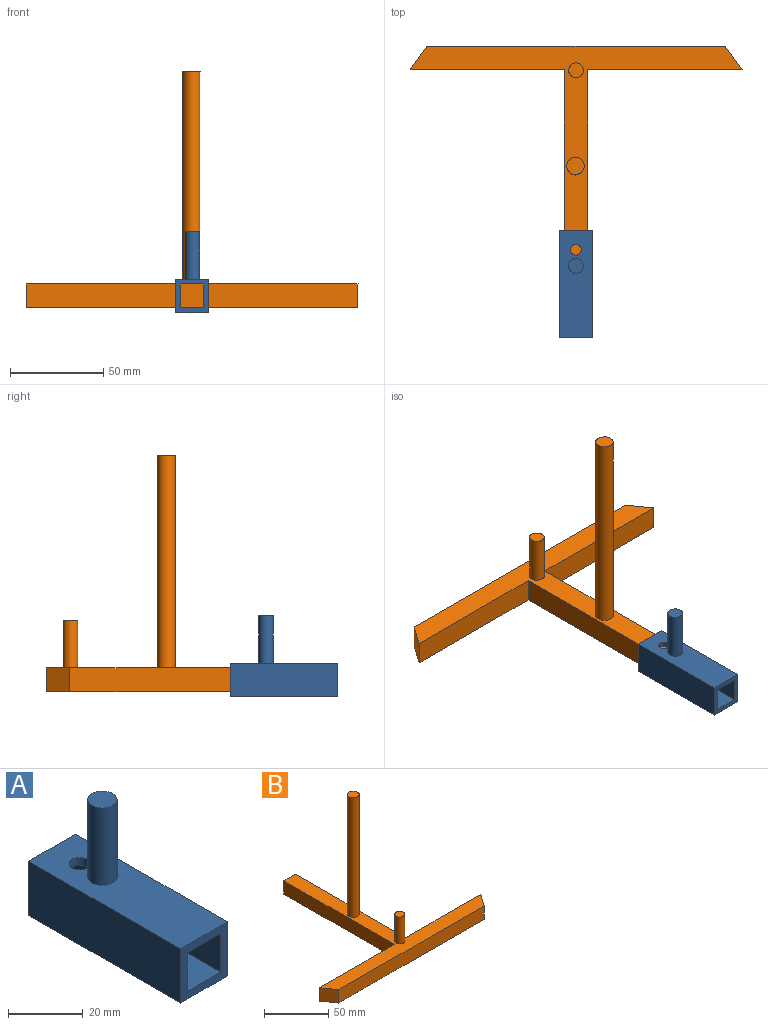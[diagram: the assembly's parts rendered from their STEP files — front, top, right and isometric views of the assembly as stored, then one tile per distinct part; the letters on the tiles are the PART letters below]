
ASSEMBLY  parts=2 mates=1
PART A: 13 faces, bbox 17.8x57.7x43.2 mm
  f0: plane 57.66x12.7mm, normal (0,0,-1), area 706.4mm2, adj f1,f7,f8,f9,f12
  f1: plane 57.66x12.7mm, normal (-1,0,0), area 732.3mm2, adj f0,f2,f8,f9
  f2: plane 57.66x12.7mm, normal (0,0,1), area 732.3mm2, adj f1,f7,f8,f9
  f3: plane 57.66x17.78mm, normal (0,0,1), area 950mm2, adj f4,f6,f8,f9,f10,f12
  f4: plane 57.66x17.78mm, normal (-1,0,0), area 1025.2mm2, adj f3,f5,f8,f9
  f5: plane 57.66x17.78mm, normal (0,0,-1), area 1025.2mm2, adj f4,f6,f8,f9
  f6: plane 57.66x17.78mm, normal (1,0,0), area 1025.2mm2, adj f3,f5,f8,f9
  f7: plane 57.66x12.7mm, normal (1,0,0), area 732.3mm2, adj f0,f2,f8,f9
  f8: plane 17.78x17.78mm, normal (0,-1,0), area 154.8mm2, adj f0,f1,f2,f3,f4,f5,f6,f7
  f9: plane 17.78x17.78mm, normal (0,1,0), area 154.8mm2, adj f0,f1,f2,f3,f4,f5,f6,f7
  f10: cylinder r=3.96mm len=25.4mm, axis (0,0,-1), area 631.9mm2, adj f3,f11
  f11: plane 7.92x7.92mm, normal (0,0,1), area 49.3mm2, adj f10
  f12: cylinder r=2.87mm len=5.74mm, axis (0,0,1), area 45.8mm2, adj f0,f3
PART B: 14 faces, bbox 177.8x134.2x126.5 mm
  f0: plane 82.57x12.7mm, normal (0,1,0), area 1048.6mm2, adj f1,f7,f8,f9
  f1: plane 121.46x12.7mm, normal (1,0,0), area 1542.6mm2, adj f0,f2,f8,f9
  f2: plane 12.7x12.7mm, normal (0,1,0), area 161.3mm2, adj f1,f3,f8,f9
  f3: plane 121.46x12.7mm, normal (-1,0,0), area 1542.6mm2, adj f2,f4,f8,f9
  f4: plane 82.57x12.7mm, normal (0,1,0), area 1048.6mm2, adj f3,f5,f8,f9
  f5: plane 12.7x12.7mm, normal (-0.82,-0.58,0), area 197.5mm2, adj f4,f6,f8,f9
  f6: plane 159.88x12.7mm, normal (0,-1,0), area 2030.5mm2, adj f5,f7,f8,f9
  f7: plane 12.7x12.7mm, normal (0.82,-0.58,0), area 197.5mm2, adj f0,f6,f8,f9
  f8: plane 177.84x134.16mm, normal (0,0,1), area 3570mm2, adj f0,f1,f2,f3,f4,f5,f6,f7
  f9: plane 177.84x134.16mm, normal (0,0,-1), area 3687.1mm2, adj f0,f1,f2,f3,f4,f5,f6,f7
  f10: cylinder r=4.67mm len=113.79mm, axis (0,0,-1), area 3337mm2, adj f8,f11
  f11: plane 9.33x9.33mm, normal (0,0,1), area 68.4mm2, adj f10
  f12: cylinder r=3.94mm len=25.4mm, axis (0,0,-1), area 628mm2, adj f8,f13
  f13: plane 7.87x7.87mm, normal (0,0,1), area 48.7mm2, adj f12
PLACE A t=(-8,-103.93,-12.59)mm
PLACE B rot(axis=(0,0,-1),180deg) t=(-8,-38.78,-18.94)mm fixed
MATE slider B.f2 <-> A.f9  axis (0,-1,0) through (-8,-126.79,-12.59)mm
